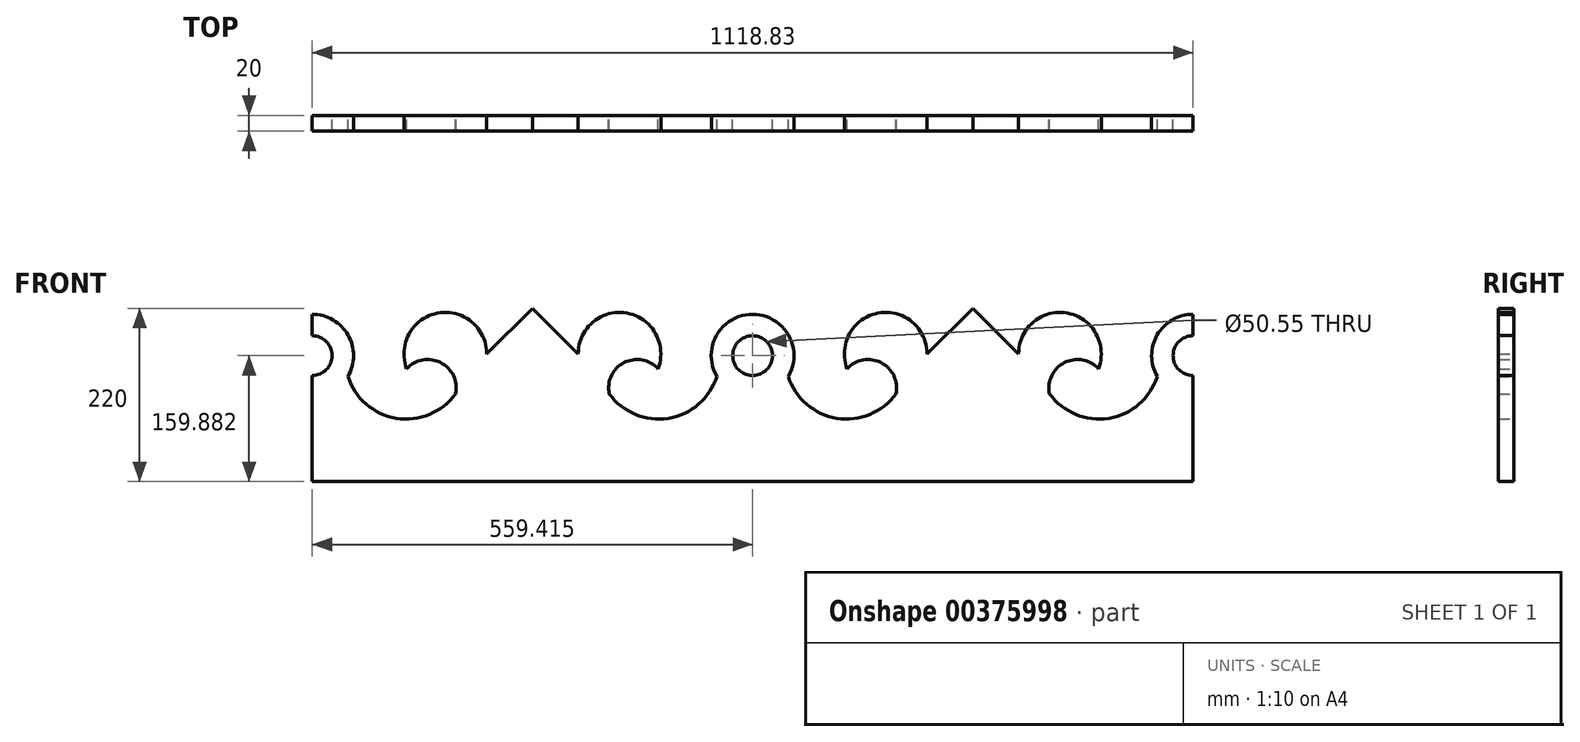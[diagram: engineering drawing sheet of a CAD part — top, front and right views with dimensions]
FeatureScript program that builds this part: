
annotation { "Feature Type Name" : "Feature", "Feature Type Description" : "" }
export const myFeature = defineFeature(function(context is Context, id is Id, definition is map)
    precondition{}
    {
        {
            var Q0;
            Q0=qCreatedBy(makeId("Front.planeOp"),FACE);
            var sketch = newSketch(context, id + "F0", { "sketchPlane" : qUnion([Q0])});
            skLineSegment(sketch, "E0", {"start": v(-23.66, 0) * mm, "end": v(-523.66, 0) * mm});
            skLineSegment(sketch, "E1", {"start": v(-523.66, 0) * mm, "end": v(-523.66, 134.6) * mm});
            skArc(sketch, "E2", {"start": v(-302.11, 162.23) * mm, "mid": v(-364.32, 213.83) * mm, "end": v(-403.53, 143.16) * mm});
            skPoint(sketch, "E2.first.point", {"position": v(-403.53, 143.16) * mm});
            skPoint(sketch, "E2.second.point", {"position": v(-352.54, 214.7) * mm});
            skLineSegment(sketch, "E3", {"start": v(-243.95, 220) * mm, "end": v(-302.11, 162.23) * mm});
            skArc(sketch, "E4", {"start": v(-478.3, 133.45) * mm, "mid": v(-478.14, 186.04) * mm, "end": v(-523.66, 212.38) * mm});
            skArc(sketch, "E5", {"start": v(-523.66, 134.6) * mm, "mid": v(-498.38, 159.88) * mm, "end": v(-523.66, 185.16) * mm});
            skArc(sketch, "E6", {"start": v(-478.3, 133.45) * mm, "mid": v(-416.67, 80.3) * mm, "end": v(-341.47, 111.4) * mm});
            skArc(sketch, "E7", {"start": v(-341.47, 111.4) * mm, "mid": v(-360.4, 150.93) * mm, "end": v(-403.53, 143.16) * mm});
            skPoint(sketch, "E8", {"position": v(-523.66, 212.38) * mm});
            skPoint(sketch, "E9", {"position": v(-523.66, 185.16) * mm});
            skPoint(sketch, "E10", {"position": v(-523.66, 134.6) * mm});
            skPoint(sketch, "E11", {"position": v(-523.66, 107.38) * mm});
            skLineSegment(sketch, "E12", {"start": v(-243.95, 220) * mm, "end": v(-243.95, 0) * mm});
            skPoint(sketch, "E13.MirrorP", {"position": v(35.76, 134.6) * mm});
            skPoint(sketch, "E14.MirrorP", {"position": v(35.76, 212.38) * mm});
            skPoint(sketch, "E15.MirrorP", {"position": v(-135.35, 214.7) * mm});
            skArc(sketch, "E16.MirrorCS", {"start": v(-185.78, 162.23) * mm, "mid": v(-123.58, 213.83) * mm, "end": v(-84.37, 143.16) * mm});
            skLineSegment(sketch, "E17.MirrorCS", {"start": v(-243.95, 220) * mm, "end": v(-185.78, 162.23) * mm});
            skArc(sketch, "E18.MirrorCS", {"start": v(-9.6, 133.45) * mm, "mid": v(-9.76, 186.04) * mm, "end": v(35.76, 212.38) * mm});
            skArc(sketch, "E19.MirrorCS", {"start": v(35.76, 134.6) * mm, "mid": v(10.48, 159.88) * mm, "end": v(35.76, 185.16) * mm});
            skArc(sketch, "E20.MirrorCS", {"start": v(-9.6, 133.45) * mm, "mid": v(-71.23, 80.3) * mm, "end": v(-146.43, 111.4) * mm});
            skArc(sketch, "E21.MirrorCS", {"start": v(-146.43, 111.4) * mm, "mid": v(-127.5, 150.93) * mm, "end": v(-84.37, 143.16) * mm});
            skPoint(sketch, "E22.MirrorP", {"position": v(35.76, 185.16) * mm});
            skPoint(sketch, "E23.MirrorP", {"position": v(35.76, 107.38) * mm});
            skLineSegment(sketch, "E24.MirrorCS", {"start": v(-464.24, 0) * mm, "end": v(35.76, 0) * mm});
            skPoint(sketch, "E25.MirrorP", {"position": v(-84.37, 143.16) * mm});
            skLineSegment(sketch, "E26.MirrorCS", {"start": v(35.76, 0) * mm, "end": v(35.76, 134.6) * mm});
            skLineSegment(sketch, "E27.trimOffspring", {"start": v(-523.66, 185.16) * mm, "end": v(-523.66, 220) * mm});
            skLineSegment(sketch, "E28.trimOffspring", {"start": v(35.76, 185.16) * mm, "end": v(35.76, 220) * mm});
            skLineSegment(sketch, "E29.MirrorCS", {"start": v(-1083.07, 185.16) * mm, "end": v(-1083.07, 220) * mm});
            skPoint(sketch, "E30.MirrorP", {"position": v(-694.77, 214.7) * mm});
            skPoint(sketch, "E31.MirrorP", {"position": v(-911.96, 214.7) * mm});
            skArc(sketch, "E32.MirrorCS", {"start": v(-745.2, 162.23) * mm, "mid": v(-683, 213.83) * mm, "end": v(-643.78, 143.16) * mm});
            skArc(sketch, "E33.MirrorCS", {"start": v(-1083.07, 134.6) * mm, "mid": v(-1057.8, 159.88) * mm, "end": v(-1083.07, 185.16) * mm});
            skLineSegment(sketch, "E34.MirrorCS", {"start": v(-803.36, 220) * mm, "end": v(-745.2, 162.23) * mm});
            skArc(sketch, "E35.MirrorCS", {"start": v(-569.02, 133.45) * mm, "mid": v(-569.17, 186.04) * mm, "end": v(-523.66, 212.38) * mm});
            skArc(sketch, "E36.MirrorCS", {"start": v(-523.66, 134.6) * mm, "mid": v(-548.93, 159.88) * mm, "end": v(-523.66, 185.16) * mm});
            skArc(sketch, "E37.MirrorCS", {"start": v(-569.02, 133.45) * mm, "mid": v(-630.64, 80.3) * mm, "end": v(-705.84, 111.4) * mm});
            skArc(sketch, "E38.MirrorCS", {"start": v(-1037.7, 133.45) * mm, "mid": v(-1037.55, 186.04) * mm, "end": v(-1083.07, 212.38) * mm});
            skPoint(sketch, "E39.MirrorP", {"position": v(-962.94, 143.16) * mm});
            skLineSegment(sketch, "E40.MirrorCS", {"start": v(-583.07, 0) * mm, "end": v(-1083.07, 0) * mm});
            skArc(sketch, "E41.MirrorCS", {"start": v(-705.84, 111.4) * mm, "mid": v(-686.91, 150.93) * mm, "end": v(-643.78, 143.16) * mm});
            skPoint(sketch, "E42.MirrorP", {"position": v(-1083.07, 212.38) * mm});
            skArc(sketch, "E43.MirrorCS", {"start": v(-861.53, 162.23) * mm, "mid": v(-923.73, 213.83) * mm, "end": v(-962.94, 143.16) * mm});
            skLineSegment(sketch, "E44.MirrorCS", {"start": v(-803.36, 220) * mm, "end": v(-803.36, 0) * mm});
            skArc(sketch, "E45.MirrorCS", {"start": v(-900.88, 111.4) * mm, "mid": v(-919.81, 150.93) * mm, "end": v(-962.94, 143.16) * mm});
            skArc(sketch, "E46.MirrorCS", {"start": v(-1037.7, 133.45) * mm, "mid": v(-976.08, 80.3) * mm, "end": v(-900.88, 111.4) * mm});
            skLineSegment(sketch, "E47.MirrorCS", {"start": v(-803.36, 220) * mm, "end": v(-861.53, 162.23) * mm});
            skLineSegment(sketch, "E48.MirrorCS", {"start": v(-1023.66, 0) * mm, "end": v(-523.66, 0) * mm});
            skPoint(sketch, "E49.MirrorP", {"position": v(-1083.07, 107.38) * mm});
            skPoint(sketch, "E50.MirrorP", {"position": v(-1083.07, 134.6) * mm});
            skPoint(sketch, "E51.MirrorP", {"position": v(-1083.07, 185.16) * mm});
            skLineSegment(sketch, "E52.MirrorCS", {"start": v(-1083.07, 0) * mm, "end": v(-1083.07, 134.6) * mm});
            skPoint(sketch, "E53.MirrorP", {"position": v(-643.78, 143.16) * mm});
            skSolve(sketch);
        }
        {
            var Q0;
            Q0 = qSketchRegion(id + "F0", true);
            extrude(context, id + "F1", {"entities" : qUnion([Q0]), "depth" : 20 * mm});
        }
    });
